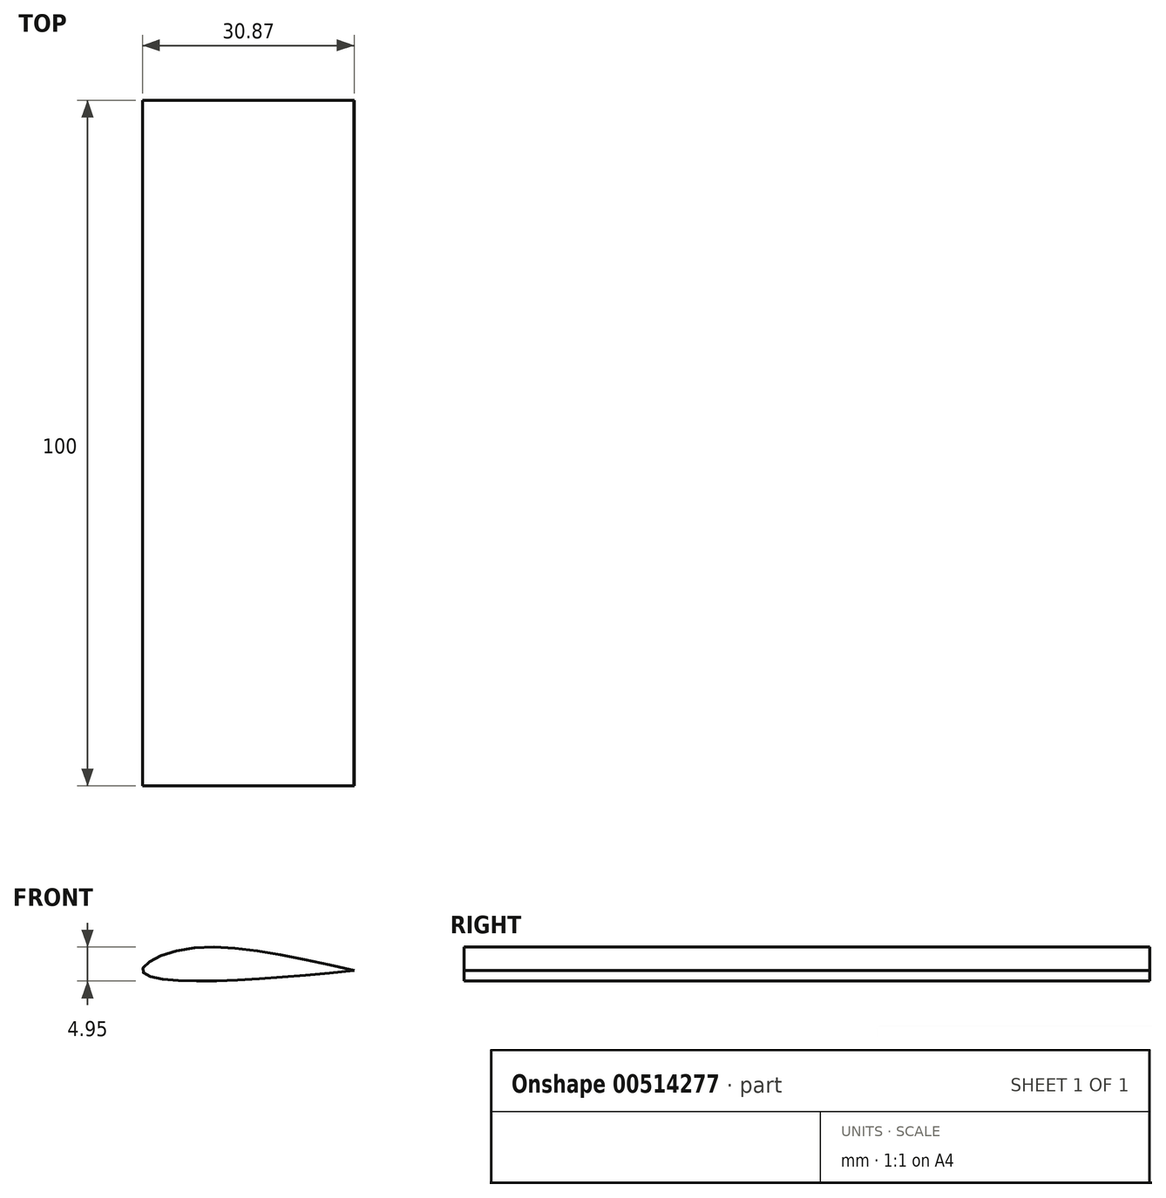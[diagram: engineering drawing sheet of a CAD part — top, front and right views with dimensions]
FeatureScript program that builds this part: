
annotation { "Feature Type Name" : "Feature", "Feature Type Description" : "" }
export const myFeature = defineFeature(function(context is Context, id is Id, definition is map)
    precondition{}
    {
        {
            var Q0;
            Q0=qCreatedBy(makeId("Front.planeOp"),FACE);
            var sketch = newSketch(context, id + "F0", { "sketchPlane" : qUnion([Q0])});
            skFitSpline(sketch, "E0", {"points": [v(18.77, 0) * mm, v(-5.47, -1.49) * mm, v(-12.03, 0) * mm, v(-6.16, 3.08) * mm, v(18.84, 0) * mm], "startDerivative": vector(-80.83, -7.85) * mm, "endDerivative": vector(83.42, -19.4) * mm});
            skLineSegment(sketch, "E1", {"start": v(18.77, 0) * mm, "end": v(18.84, 0) * mm});
            skSolve(sketch);
        }
        {
            var Q0;
            Q0=makeQuery(id+"F0.imprint","IMPRINT",FACE,{"disambiguationData":[TD([[makeQuery(id+"F0.imprint","IMPRINT",EDGE,{"derivedFrom":sQuery(id+"F0.wireOp",EDGE,"E0")}),-1.0]])]});
            extrude(context, id + "F1", {"entities" : qUnion([Q0]), "depth" : 100 * mm, "symmetric" : true});
        }
    });
